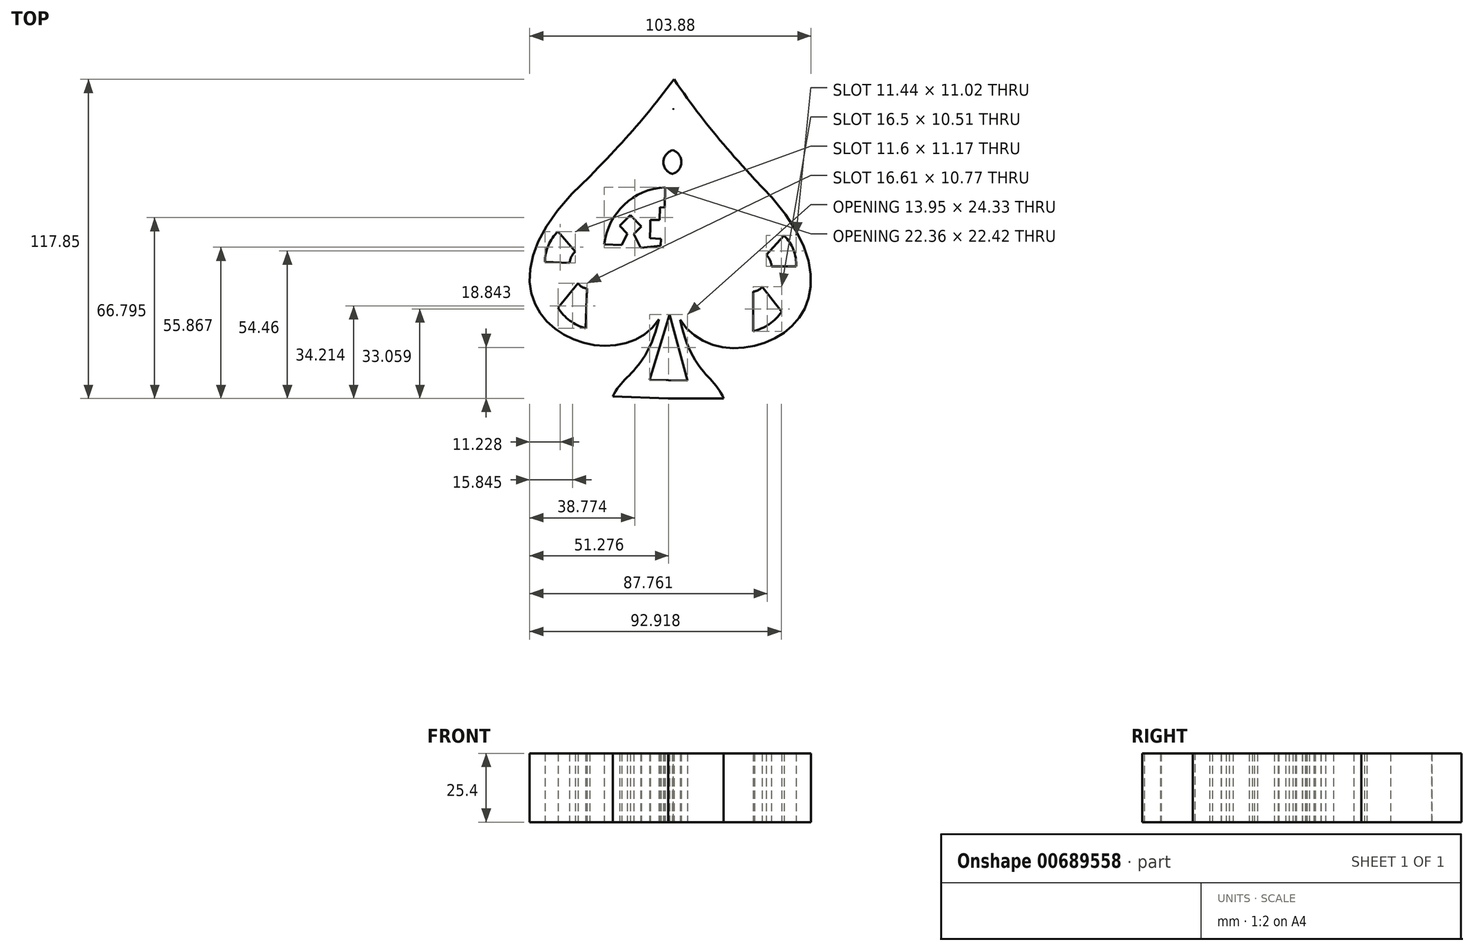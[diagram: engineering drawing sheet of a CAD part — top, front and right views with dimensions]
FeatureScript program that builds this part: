
annotation { "Feature Type Name" : "Feature", "Feature Type Description" : "" }
export const myFeature = defineFeature(function(context is Context, id is Id, definition is map)
    precondition{}
    {
        {
            var Q0;
            Q0=qCreatedBy(makeId("Top.planeOp"),FACE);
            var sketch = newSketch(context, id + "F0", { "sketchPlane" : qUnion([Q0])});
            skFitSpline(sketch, "E0", {"points": [v(-2.53, -37.9) * mm, v(-18.56, -8.8) * mm], "startDerivative": vector(-10, 25.18) * mm, "endDerivative": vector(-11.98, 58.7) * mm});
            skFitSpline(sketch, "E1", {"points": [v(-18.56, -8.8) * mm, v(8.92, 43.01) * mm], "startDerivative": vector(48.1, -79.64) * mm, "endDerivative": vector(-160.88, 156.33) * mm});
            skFitSpline(sketch, "E2", {"points": [v(8.92, 43.01) * mm, v(-20.9, 79.96) * mm], "startDerivative": vector(-37.04, 40.28) * mm, "endDerivative": vector(-28.87, 41.7) * mm});
            skLineSegment(sketch, "E3", {"start": v(-73.33, 8.06) * mm, "end": v(29.07, 0) * mm, "construction": true});
            skLineSegment(sketch, "E4", {"start": v(-2.53, -37.9) * mm, "end": v(-43.46, -37.9) * mm, "construction": true});
            skLineSegment(sketch, "E5", {"start": v(-23, -37.9) * mm, "end": v(-2.53, -37.9) * mm});
            skLineSegment(sketch, "E6", {"start": v(-23, -37.9) * mm, "end": v(-20.9, 79.96) * mm, "construction": true});
            skFitSpline(sketch, "E7.MirrorCS", {"points": [v(-52, 44.1) * mm, v(-20.9, 79.96) * mm], "startDerivative": vector(38.45, 38.94) * mm, "endDerivative": vector(30.34, 40.65) * mm});
            skFitSpline(sketch, "E8.MirrorCS", {"points": [v(-26.39, -8.66) * mm, v(-52, 44.1) * mm], "startDerivative": vector(-50.9, -77.88) * mm, "endDerivative": vector(166.34, 150.5) * mm});
            skFitSpline(sketch, "E9.MirrorCS", {"points": [v(-43.45, -37.16) * mm, v(-26.39, -8.66) * mm], "startDerivative": vector(10.89, 24.8) * mm, "endDerivative": vector(14.06, 58.23) * mm});
            skLineSegment(sketch, "E10.MirrorCS", {"start": v(-23, -37.9) * mm, "end": v(-43.45, -37.16) * mm});
            skFitSpline(sketch, "E11", {"points": [v(-22.32, 0) * mm, v(7.76, 41.99) * mm], "startDerivative": vector(35, -98.07) * mm, "endDerivative": vector(-155.79, 159.42) * mm});
            skLineSegment(sketch, "E12", {"start": v(7.76, 41.99) * mm, "end": v(-20.97, 75.69) * mm});
            skFitSpline(sketch, "E13.MirrorCS", {"points": [v(-22.32, 0) * mm, v(-50.89, 43.03) * mm], "startDerivative": vector(-38.47, -96.76) * mm, "endDerivative": vector(161.36, 153.78) * mm});
            skLineSegment(sketch, "E14.MirrorCS", {"start": v(-50.89, 43.03) * mm, "end": v(-20.97, 75.69) * mm});
            skFitSpline(sketch, "E15", {"points": [v(-21.1, 69) * mm, v(-12.63, 48.2) * mm], "startDerivative": vector(-3.17, 1.85) * mm, "endDerivative": vector(-12.5, -47.35) * mm});
            skFitSpline(sketch, "E16", {"points": [v(-12.63, 48.2) * mm, v(4.86, 35.93) * mm], "startDerivative": vector(24.47, -10.82) * mm, "endDerivative": vector(17.62, -20.68) * mm});
            skLineSegment(sketch, "E17", {"start": v(4.86, 35.93) * mm, "end": v(8.75, 35.43) * mm});
            skLineSegment(sketch, "E18", {"start": v(8.75, 35.43) * mm, "end": v(12.5, 31.25) * mm});
            skFitSpline(sketch, "E19", {"points": [v(12.5, 31.25) * mm, v(4.93, -2.27) * mm], "startDerivative": vector(-13.3, -42.42) * mm, "endDerivative": vector(-3.8, -40.26) * mm});
            skLineSegment(sketch, "E20", {"start": v(4.93, -2.27) * mm, "end": v(-17.9, -2.27) * mm});
            skLineSegment(sketch, "E21", {"start": v(-17.9, -2.27) * mm, "end": v(-22.3, 1.14) * mm});
            skLineSegment(sketch, "E22", {"start": v(-22.3, 1.14) * mm, "end": v(1.58, 0.9) * mm});
            skFitSpline(sketch, "E23", {"points": [v(1.58, 0.9) * mm, v(9.1, 30.71) * mm], "startDerivative": vector(0.02, 34.28) * mm, "endDerivative": vector(0.64, 27.66) * mm});
            skLineSegment(sketch, "E24", {"start": v(9.1, 30.71) * mm, "end": v(3.9, 31.77) * mm});
            skFitSpline(sketch, "E25", {"points": [v(3.9, 31.77) * mm, v(-17.82, 45.13) * mm], "startDerivative": vector(-2.54, 4.45) * mm, "endDerivative": vector(-44.2, 0.64) * mm});
            skFitSpline(sketch, "E26", {"points": [v(-17.82, 45.13) * mm, v(-19.45, 54.64) * mm], "startDerivative": vector(6.8, 6.6) * mm, "endDerivative": vector(-16.6, 7.97) * mm});
            skFitSpline(sketch, "E27", {"points": [v(-19.45, 54.64) * mm, v(-18.91, 55.61) * mm], "startDerivative": vector(1.1, 0.75) * mm, "endDerivative": vector(0.26, 1.43) * mm});
            skLineSegment(sketch, "E28", {"start": v(-18.91, 55.61) * mm, "end": v(-15.88, 55.02) * mm});
            skLineSegment(sketch, "E29", {"start": v(-15.88, 55.02) * mm, "end": v(-15.16, 58.67) * mm});
            skLineSegment(sketch, "E30", {"start": v(-15.16, 58.67) * mm, "end": v(-16.2, 58.69) * mm});
            skLineSegment(sketch, "E31", {"start": v(-16.2, 58.69) * mm, "end": v(-16.2, 60.6) * mm});
            skLineSegment(sketch, "E32", {"start": v(-16.2, 60.6) * mm, "end": v(-17.81, 60.63) * mm});
            skLineSegment(sketch, "E33", {"start": v(-17.81, 60.63) * mm, "end": v(-17.71, 62.36) * mm});
            skLineSegment(sketch, "E34", {"start": v(-17.71, 62.36) * mm, "end": v(-19.06, 62.48) * mm});
            skLineSegment(sketch, "E35", {"start": v(-19.06, 62.48) * mm, "end": v(-19.06, 64.14) * mm});
            skLineSegment(sketch, "E36", {"start": v(-19.06, 64.14) * mm, "end": v(-21.17, 64.57) * mm});
            skLineSegment(sketch, "E37.MirrorCS", {"start": v(-23.3, 64.21) * mm, "end": v(-21.17, 64.57) * mm});
            skLineSegment(sketch, "E38.MirrorCS", {"start": v(-23.35, 62.55) * mm, "end": v(-23.3, 64.21) * mm});
            skLineSegment(sketch, "E39.MirrorCS", {"start": v(-24.7, 62.49) * mm, "end": v(-23.35, 62.55) * mm});
            skLineSegment(sketch, "E40.MirrorCS", {"start": v(-24.67, 60.75) * mm, "end": v(-24.7, 62.49) * mm});
            skLineSegment(sketch, "E41.MirrorCS", {"start": v(-26.29, 60.78) * mm, "end": v(-24.67, 60.75) * mm});
            skLineSegment(sketch, "E42.MirrorCS", {"start": v(-26.36, 58.87) * mm, "end": v(-26.29, 60.78) * mm});
            skLineSegment(sketch, "E43.MirrorCS", {"start": v(-27.38, 58.89) * mm, "end": v(-26.36, 58.87) * mm});
            skLineSegment(sketch, "E44.MirrorCS", {"start": v(-26.8, 55.21) * mm, "end": v(-27.38, 58.89) * mm});
            skLineSegment(sketch, "E45.MirrorCS", {"start": v(-23.75, 55.7) * mm, "end": v(-26.8, 55.21) * mm});
            skFitSpline(sketch, "E46.MirrorCS", {"points": [v(-23.24, 54.71) * mm, v(-23.75, 55.7) * mm], "startDerivative": vector(-1.07, 0.79) * mm, "endDerivative": vector(-0.2, 1.44) * mm});
            skFitSpline(sketch, "E47.MirrorCS", {"points": [v(-25.2, 45.26) * mm, v(-23.24, 54.71) * mm], "startDerivative": vector(-6.57, 6.83) * mm, "endDerivative": vector(16.88, 7.38) * mm});
            skFitSpline(sketch, "E48.MirrorCS", {"points": [v(-47.4, 32.69) * mm, v(-25.2, 45.26) * mm], "startDerivative": vector(2.7, 4.36) * mm, "endDerivative": vector(44.19, -0.94) * mm});
            skLineSegment(sketch, "E49.MirrorCS", {"start": v(-52.62, 31.81) * mm, "end": v(-47.4, 32.69) * mm});
            skFitSpline(sketch, "E50.MirrorCS", {"points": [v(-46.17, 1.74) * mm, v(-52.62, 31.81) * mm], "startDerivative": vector(1.2, 34.26) * mm, "endDerivative": vector(0.35, 27.66) * mm});
            skLineSegment(sketch, "E51.MirrorCS", {"start": v(-22.3, 1.14) * mm, "end": v(-46.17, 1.74) * mm});
            skLineSegment(sketch, "E52.MirrorCS", {"start": v(-26.81, -2.11) * mm, "end": v(-22.3, 1.14) * mm});
            skLineSegment(sketch, "E53.MirrorCS", {"start": v(-49.63, -1.3) * mm, "end": v(-26.81, -2.11) * mm});
            skFitSpline(sketch, "E54.MirrorCS", {"points": [v(-56.01, 32.47) * mm, v(-49.63, -1.3) * mm], "startDerivative": vector(11.78, -42.87) * mm, "endDerivative": vector(2.37, -40.37) * mm});
            skLineSegment(sketch, "E55.MirrorCS", {"start": v(-52.1, 36.52) * mm, "end": v(-56.01, 32.47) * mm});
            skLineSegment(sketch, "E56.MirrorCS", {"start": v(-48.2, 36.87) * mm, "end": v(-52.1, 36.52) * mm});
            skFitSpline(sketch, "E57.MirrorCS", {"points": [v(-30.29, 48.51) * mm, v(-48.2, 36.87) * mm], "startDerivative": vector(-24.84, -9.94) * mm, "endDerivative": vector(-18.34, -20.04) * mm});
            skFitSpline(sketch, "E58.MirrorCS", {"points": [v(-21.1, 69) * mm, v(-30.29, 48.51) * mm], "startDerivative": vector(3.23, 1.74) * mm, "endDerivative": vector(10.81, -47.77) * mm});
            skArc(sketch, "E59", {"start": v(-21.52, 45) * mm, "mid": v(-18.12, 49.33) * mm, "end": v(-21.36, 53.79) * mm});
            skArc(sketch, "E60", {"start": v(2.89, 29.49) * mm, "mid": v(-7.22, 40.2) * mm, "end": v(-21.54, 43.65) * mm});
            skLineSegment(sketch, "E61", {"start": v(2.89, 29.49) * mm, "end": v(6.98, 28.8) * mm});
            skLineSegment(sketch, "E62", {"start": v(6.98, 28.8) * mm, "end": v(6.61, 27) * mm});
            skLineSegment(sketch, "E63", {"start": v(6.61, 27) * mm, "end": v(2.1, 27.63) * mm});
            skArc(sketch, "E64", {"start": v(2.1, 27.63) * mm, "mid": v(-7.57, 38.43) * mm, "end": v(-21.57, 42.2) * mm});
            skLineSegment(sketch, "E65", {"start": v(-19.02, 40.02) * mm, "end": v(-19.15, 32.56) * mm});
            skLineSegment(sketch, "E66", {"start": v(-19.15, 32.56) * mm, "end": v(-17.43, 32.53) * mm});
            skLineSegment(sketch, "E67", {"start": v(-17.43, 32.53) * mm, "end": v(-17.51, 27.87) * mm});
            skLineSegment(sketch, "E68", {"start": v(-17.51, 27.87) * mm, "end": v(-14.09, 27.8) * mm});
            skLineSegment(sketch, "E69", {"start": v(-14.09, 27.8) * mm, "end": v(-14.14, 25.18) * mm});
            skLineSegment(sketch, "E70", {"start": v(-14.14, 25.18) * mm, "end": v(-14.14, 20.98) * mm});
            skLineSegment(sketch, "E71", {"start": v(-14.14, 20.98) * mm, "end": v(-18.2, 20.98) * mm});
            skLineSegment(sketch, "E72", {"start": v(-18.2, 20.98) * mm, "end": v(-18.2, 18.43) * mm});
            skLineSegment(sketch, "E73", {"start": v(-18.2, 18.43) * mm, "end": v(-10.92, 17.3) * mm});
            skLineSegment(sketch, "E74", {"start": v(-10.92, 17.3) * mm, "end": v(-8.1, 22.3) * mm});
            skLineSegment(sketch, "E75", {"start": v(-8.1, 22.3) * mm, "end": v(-10.89, 25.18) * mm});
            skLineSegment(sketch, "E76", {"start": v(-10.89, 25.18) * mm, "end": v(-6.67, 29.26) * mm});
            skLineSegment(sketch, "E77", {"start": v(-6.67, 29.26) * mm, "end": v(-2.8, 25.25) * mm});
            skLineSegment(sketch, "E78", {"start": v(-2.8, 25.25) * mm, "end": v(-5.78, 22.36) * mm});
            skLineSegment(sketch, "E79", {"start": v(-5.78, 22.36) * mm, "end": v(-3.84, 18.15) * mm});
            skLineSegment(sketch, "E80", {"start": v(-3.84, 18.15) * mm, "end": v(2.58, 18.15) * mm});
            skArc(sketch, "E81", {"start": v(2.58, 18.15) * mm, "mid": v(-4.22, 33.04) * mm, "end": v(-19.02, 40.02) * mm});
            skArc(sketch, "E82.MirrorCS", {"start": v(-46.46, 30.37) * mm, "mid": v(-35.98, 40.72) * mm, "end": v(-21.54, 43.65) * mm});
            skLineSegment(sketch, "E83.MirrorCS", {"start": v(-46.46, 30.37) * mm, "end": v(-50.58, 29.82) * mm});
            skArc(sketch, "E84.MirrorCS", {"start": v(-21.52, 45) * mm, "mid": v(-24.76, 49.45) * mm, "end": v(-21.36, 53.79) * mm});
            skLineSegment(sketch, "E85.MirrorCS", {"start": v(-50.58, 29.82) * mm, "end": v(-50.28, 28) * mm});
            skLineSegment(sketch, "E86.MirrorCS", {"start": v(-50.28, 28) * mm, "end": v(-45.75, 28.48) * mm});
            skArc(sketch, "E87.MirrorCS", {"start": v(-45.75, 28.48) * mm, "mid": v(-35.7, 38.93) * mm, "end": v(-21.57, 42.2) * mm});
            skArc(sketch, "E88.MirrorCS", {"start": v(-46.56, 19.03) * mm, "mid": v(-39.24, 33.67) * mm, "end": v(-24.2, 40.12) * mm});
            skLineSegment(sketch, "E89.MirrorCS", {"start": v(-24.2, 40.12) * mm, "end": v(-24.33, 32.65) * mm});
            skLineSegment(sketch, "E90.MirrorCS", {"start": v(-24.33, 32.65) * mm, "end": v(-26.05, 32.68) * mm});
            skLineSegment(sketch, "E91.MirrorCS", {"start": v(-26.05, 32.68) * mm, "end": v(-26.13, 28.02) * mm});
            skLineSegment(sketch, "E92.MirrorCS", {"start": v(-26.13, 28.02) * mm, "end": v(-29.56, 28.08) * mm});
            skLineSegment(sketch, "E93.MirrorCS", {"start": v(-29.56, 28.08) * mm, "end": v(-29.6, 25.45) * mm});
            skLineSegment(sketch, "E94.MirrorCS", {"start": v(-29.6, 25.45) * mm, "end": v(-29.75, 21.26) * mm});
            skLineSegment(sketch, "E95.MirrorCS", {"start": v(-29.75, 21.26) * mm, "end": v(-25.7, 21.12) * mm});
            skLineSegment(sketch, "E96.MirrorCS", {"start": v(-25.7, 21.12) * mm, "end": v(-25.8, 18.57) * mm});
            skLineSegment(sketch, "E97.MirrorCS", {"start": v(-25.8, 18.57) * mm, "end": v(-33.1, 17.7) * mm});
            skLineSegment(sketch, "E98.MirrorCS", {"start": v(-33.1, 17.7) * mm, "end": v(-35.74, 22.8) * mm});
            skLineSegment(sketch, "E99.MirrorCS", {"start": v(-35.74, 22.8) * mm, "end": v(-32.85, 25.57) * mm});
            skLineSegment(sketch, "E100.MirrorCS", {"start": v(-32.85, 25.57) * mm, "end": v(-36.92, 29.8) * mm});
            skLineSegment(sketch, "E101.MirrorCS", {"start": v(-36.92, 29.8) * mm, "end": v(-40.93, 25.93) * mm});
            skLineSegment(sketch, "E102.MirrorCS", {"start": v(-40.93, 25.93) * mm, "end": v(-38.05, 22.93) * mm});
            skLineSegment(sketch, "E103.MirrorCS", {"start": v(-38.05, 22.93) * mm, "end": v(-40.14, 18.8) * mm});
            skLineSegment(sketch, "E104.MirrorCS", {"start": v(-40.14, 18.8) * mm, "end": v(-46.56, 19.03) * mm});
            skLineSegment(sketch, "E105.bottom", {"start": v(-22.06, 14.7) * mm, "end": v(0.65, 14.7) * mm});
            skLineSegment(sketch, "E105.top", {"start": v(-22.06, 9.84) * mm, "end": v(0.65, 9.84) * mm});
            skLineSegment(sketch, "E105.right", {"start": v(0.65, 14.7) * mm, "end": v(0.65, 9.84) * mm});
            skLineSegment(sketch, "E106.bottom", {"start": v(-22.2, 7.26) * mm, "end": v(0, 7.26) * mm});
            skLineSegment(sketch, "E106.top", {"start": v(-22.28, 2.29) * mm, "end": v(0, 2.29) * mm});
            skLineSegment(sketch, "E106.right", {"start": v(0, 7.26) * mm, "end": v(0, 2.29) * mm});
            skLineSegment(sketch, "E107.MirrorCS", {"start": v(-22.06, 14.7) * mm, "end": v(-44.76, 15.5) * mm});
            skLineSegment(sketch, "E108.MirrorCS", {"start": v(-22.23, 9.85) * mm, "end": v(-44.93, 10.66) * mm});
            skLineSegment(sketch, "E109.MirrorCS", {"start": v(-22.2, 7.26) * mm, "end": v(-44.37, 8.05) * mm});
            skLineSegment(sketch, "E110.MirrorCS", {"start": v(-22.28, 2.29) * mm, "end": v(-44.55, 3.08) * mm});
            skLineSegment(sketch, "E111.MirrorCS", {"start": v(-44.37, 8.05) * mm, "end": v(-44.55, 3.08) * mm});
            skLineSegment(sketch, "E112.MirrorCS", {"start": v(-44.76, 15.5) * mm, "end": v(-44.93, 10.66) * mm});
            skLineSegment(sketch, "E113.bottom", {"start": v(-5.78, 5.45) * mm, "end": v(-1.65, 5.45) * mm});
            skLineSegment(sketch, "E113.top", {"start": v(-5.78, 4.02) * mm, "end": v(-1.65, 4.02) * mm});
            skLineSegment(sketch, "E113.left", {"start": v(-5.78, 5.45) * mm, "end": v(-5.78, 4.02) * mm});
            skLineSegment(sketch, "E113.right", {"start": v(-1.65, 5.45) * mm, "end": v(-1.65, 4.02) * mm});
            skLineSegment(sketch, "E114.bottom", {"start": v(-12.25, 5.3) * mm, "end": v(-7.48, 5.3) * mm});
            skLineSegment(sketch, "E114.top", {"start": v(-12.25, 3.82) * mm, "end": v(-7.48, 3.82) * mm});
            skLineSegment(sketch, "E114.left", {"start": v(-12.25, 5.3) * mm, "end": v(-12.25, 3.82) * mm});
            skLineSegment(sketch, "E114.right", {"start": v(-7.48, 5.3) * mm, "end": v(-7.48, 3.82) * mm});
            skLineSegment(sketch, "E115.bottom", {"start": v(-19.15, 5.33) * mm, "end": v(-14.41, 5.33) * mm});
            skLineSegment(sketch, "E115.top", {"start": v(-19.15, 3.42) * mm, "end": v(-14.41, 3.42) * mm});
            skLineSegment(sketch, "E115.left", {"start": v(-19.15, 5.33) * mm, "end": v(-19.15, 3.42) * mm});
            skLineSegment(sketch, "E115.right", {"start": v(-14.41, 5.33) * mm, "end": v(-14.41, 3.42) * mm});
            skLineSegment(sketch, "E116.MirrorCS", {"start": v(-25.3, 5.44) * mm, "end": v(-30.04, 5.61) * mm});
            skLineSegment(sketch, "E117.MirrorCS", {"start": v(-25.3, 5.44) * mm, "end": v(-25.36, 3.53) * mm});
            skLineSegment(sketch, "E118.MirrorCS", {"start": v(-25.36, 3.53) * mm, "end": v(-30.1, 3.7) * mm});
            skLineSegment(sketch, "E119.MirrorCS", {"start": v(-30.04, 5.61) * mm, "end": v(-30.1, 3.7) * mm});
            skLineSegment(sketch, "E120.MirrorCS", {"start": v(-32.2, 5.65) * mm, "end": v(-32.25, 4.18) * mm});
            skLineSegment(sketch, "E121.MirrorCS", {"start": v(-32.2, 5.65) * mm, "end": v(-36.96, 5.82) * mm});
            skLineSegment(sketch, "E122.MirrorCS", {"start": v(-36.96, 5.82) * mm, "end": v(-37.01, 4.35) * mm});
            skLineSegment(sketch, "E123.MirrorCS", {"start": v(-32.25, 4.18) * mm, "end": v(-37.01, 4.35) * mm});
            skLineSegment(sketch, "E124.MirrorCS", {"start": v(-38.66, 6.04) * mm, "end": v(-38.71, 4.6) * mm});
            skLineSegment(sketch, "E125.MirrorCS", {"start": v(-38.66, 6.04) * mm, "end": v(-42.79, 6.18) * mm});
            skLineSegment(sketch, "E126.MirrorCS", {"start": v(-42.79, 6.18) * mm, "end": v(-42.84, 4.76) * mm});
            skLineSegment(sketch, "E127.MirrorCS", {"start": v(-38.71, 4.6) * mm, "end": v(-42.84, 4.76) * mm});
            skLineSegment(sketch, "E128", {"start": v(-37.68, 15.25) * mm, "end": v(-40.35, 12.52) * mm});
            skLineSegment(sketch, "E129", {"start": v(-40.35, 12.52) * mm, "end": v(-37.68, 10.4) * mm});
            skLineSegment(sketch, "E130", {"start": v(-37.68, 10.4) * mm, "end": v(-35.15, 12.52) * mm});
            skLineSegment(sketch, "E131", {"start": v(-35.15, 12.52) * mm, "end": v(-37.68, 15.25) * mm});
            skLineSegment(sketch, "E132", {"start": v(-29.44, 13.52) * mm, "end": v(-30.94, 12.05) * mm});
            skPoint(sketch, "E132.startSnap0", {"position": v(-29.44, 18.13) * mm});
            skLineSegment(sketch, "E133", {"start": v(-30.94, 12.05) * mm, "end": v(-29.44, 10.53) * mm});
            skLineSegment(sketch, "E134", {"start": v(-29.44, 10.53) * mm, "end": v(-27.89, 12.05) * mm});
            skLineSegment(sketch, "E135", {"start": v(-27.89, 12.05) * mm, "end": v(-29.44, 13.52) * mm});
            skLineSegment(sketch, "E136.MirrorCS", {"start": v(-16.33, 11.85) * mm, "end": v(-14.72, 13.26) * mm});
            skLineSegment(sketch, "E137.MirrorCS", {"start": v(-14.72, 13.26) * mm, "end": v(-13.28, 11.74) * mm});
            skLineSegment(sketch, "E138.MirrorCS", {"start": v(-13.28, 11.74) * mm, "end": v(-14.83, 10.27) * mm});
            skLineSegment(sketch, "E139.MirrorCS", {"start": v(-14.83, 10.27) * mm, "end": v(-16.33, 11.85) * mm});
            skLineSegment(sketch, "E140.MirrorCS", {"start": v(-9.06, 12.06) * mm, "end": v(-6.43, 14.7) * mm});
            skLineSegment(sketch, "E141.MirrorCS", {"start": v(-6.43, 14.7) * mm, "end": v(-3.85, 11.87) * mm});
            skLineSegment(sketch, "E142.MirrorCS", {"start": v(-3.85, 11.87) * mm, "end": v(-6.6, 9.84) * mm});
            skLineSegment(sketch, "E143.MirrorCS", {"start": v(-6.6, 9.84) * mm, "end": v(-9.06, 12.06) * mm});
            skArc(sketch, "E144", {"start": v(24.28, 10.85) * mm, "mid": v(23.24, 17.03) * mm, "end": v(19.83, 22.3) * mm});
            skLineSegment(sketch, "E145", {"start": v(24.28, 10.85) * mm, "end": v(15.16, 10.85) * mm});
            skLineSegment(sketch, "E146", {"start": v(19.83, 22.3) * mm, "end": v(13.26, 15.09) * mm});
            skArc(sketch, "E147", {"start": v(15.16, 10.85) * mm, "mid": v(14.6, 13.14) * mm, "end": v(13.26, 15.09) * mm});
            skArc(sketch, "E148", {"start": v(8.35, -13.08) * mm, "mid": v(14.29, -10.45) * mm, "end": v(18.87, -5.85) * mm});
            skLineSegment(sketch, "E149", {"start": v(8.35, -13.08) * mm, "end": v(8.35, 1.63) * mm});
            skLineSegment(sketch, "E150", {"start": v(18.87, -5.85) * mm, "end": v(11.72, 3.42) * mm});
            skPoint(sketch, "E150.endSnap0", {"position": v(-16.78, 3.42) * mm});
            skArc(sketch, "E151", {"start": v(8.35, 1.63) * mm, "mid": v(10.25, 2.12) * mm, "end": v(11.72, 3.42) * mm});
            skLineSegment(sketch, "E152.MirrorCS", {"start": v(-63.7, -4.38) * mm, "end": v(-56.22, 4.63) * mm});
            skArc(sketch, "E153.MirrorCS", {"start": v(-53.44, -11.98) * mm, "mid": v(-59.28, -9.14) * mm, "end": v(-63.7, -4.38) * mm});
            skArc(sketch, "E154.MirrorCS", {"start": v(-52.92, 2.72) * mm, "mid": v(-54.8, 3.28) * mm, "end": v(-56.22, 4.63) * mm});
            skLineSegment(sketch, "E155.MirrorCS", {"start": v(-53.44, -11.98) * mm, "end": v(-52.92, 2.72) * mm});
            skLineSegment(sketch, "E156.MirrorCS", {"start": v(-68.5, 12.5) * mm, "end": v(-59.4, 12.18) * mm});
            skArc(sketch, "E157.MirrorCS", {"start": v(-59.4, 12.18) * mm, "mid": v(-58.75, 14.45) * mm, "end": v(-57.34, 16.34) * mm});
            skLineSegment(sketch, "E158.MirrorCS", {"start": v(-63.65, 23.78) * mm, "end": v(-57.34, 16.34) * mm});
            skArc(sketch, "E159.MirrorCS", {"start": v(-68.5, 12.5) * mm, "mid": v(-67.25, 18.64) * mm, "end": v(-63.65, 23.78) * mm});
            skLineSegment(sketch, "E160", {"start": v(-23.48, -32.5) * mm, "end": v(-22.9, -32.5) * mm});
            skLineSegment(sketch, "E161.MirrorCS", {"start": v(-22.32, -32.51) * mm, "end": v(-22.9, -32.5) * mm});
            skLineSegment(sketch, "E162", {"start": v(-22.44, -6.88) * mm, "end": v(-15.9, -31.2) * mm});
            skLineSegment(sketch, "E163", {"start": v(-15.9, -31.2) * mm, "end": v(-22.87, -31.09) * mm});
            skLineSegment(sketch, "E164.MirrorCS", {"start": v(-22.44, -6.88) * mm, "end": v(-29.85, -30.96) * mm});
            skLineSegment(sketch, "E165.MirrorCS", {"start": v(-29.85, -30.96) * mm, "end": v(-22.87, -31.09) * mm});
            skSolve(sketch);
        }
        {
            var Q0;
            Q0=makeQuery(id+"F0.imprint","IMPRINT",FACE,{"disambiguationData":[TD([[makeQuery(id+"F0.imprint","IMPRINT",EDGE,{"derivedFrom":sQuery(id+"F0.wireOp",EDGE,"TR8coMyy-DoK1-fhJf-mkVZ-P4jdJu8iWF87")}),-1.0]])]});
            var Q1;
            Q1=makeQuery(id+"F0.imprint","IMPRINT",FACE,{"disambiguationData":[TD([[makeQuery(id+"F0.imprint","IMPRINT",EDGE,{"derivedFrom":sQuery(id+"F0.wireOp",EDGE,"E11")}),1.0]])]});
            var Q2;
            Q2=makeQuery(id+"F0.imprint","IMPRINT",FACE,{"disambiguationData":[TD([[makeQuery(id+"F0.imprint","IMPRINT",EDGE,{"derivedFrom":sQuery(id+"F0.wireOp",EDGE,"E22")}),1.0]])]});
            var Q3;
            Q3=makeQuery(id+"F0.imprint","IMPRINT",FACE,{"disambiguationData":[TD([[makeQuery(id+"F0.imprint","IMPRINT",EDGE,{"derivedFrom":sQuery(id+"F0.wireOp",EDGE,"E113.bottom")}),-1.0]])]});
            var Q4;
            Q4=makeQuery(id+"F0.imprint","IMPRINT",FACE,{"disambiguationData":[TD([[makeQuery(id+"F0.imprint","IMPRINT",EDGE,{"derivedFrom":sQuery(id+"F0.wireOp",EDGE,"E114.bottom")}),-1.0]])]});
            var Q5;
            Q5=makeQuery(id+"F0.imprint","IMPRINT",FACE,{"disambiguationData":[TD([[makeQuery(id+"F0.imprint","IMPRINT",EDGE,{"derivedFrom":sQuery(id+"F0.wireOp",EDGE,"E115.bottom")}),-1.0]])]});
            var Q6;
            Q6=makeQuery(id+"F0.imprint","IMPRINT",FACE,{"disambiguationData":[TD([[makeQuery(id+"F0.imprint","IMPRINT",EDGE,{"derivedFrom":sQuery(id+"F0.wireOp",EDGE,"E116.MirrorCS")}),1.0]])]});
            var Q7;
            Q7=makeQuery(id+"F0.imprint","IMPRINT",FACE,{"disambiguationData":[TD([[makeQuery(id+"F0.imprint","IMPRINT",EDGE,{"derivedFrom":sQuery(id+"F0.wireOp",EDGE,"E120.MirrorCS")}),-1.0]])]});
            var Q8;
            Q8=makeQuery(id+"F0.imprint","IMPRINT",FACE,{"disambiguationData":[TD([[makeQuery(id+"F0.imprint","IMPRINT",EDGE,{"derivedFrom":sQuery(id+"F0.wireOp",EDGE,"E124.MirrorCS")}),-1.0]])]});
            var Q9;
            Q9=makeQuery(id+"F0.imprint","IMPRINT",FACE,{"disambiguationData":[TD([[makeQuery(id+"F0.imprint","IMPRINT",EDGE,{"derivedFrom":sQuery(id+"F0.wireOp",EDGE,"E0")}),1.0]])]});
            var Q10;
            {var subQ0=sQuery(id+"F0.wireOp",EDGE,"E16");Q10=makeQuery(id+"F0.imprint","IMPRINT",FACE,{"disambiguationData":[TD([[makeQuery(id+"F0.imprint","IMPRINT",EDGE,{"derivedFrom":subQ0}),-1.0]])]});}
            var Q11;
            Q11=makeQuery(id+"F0.imprint","IMPRINT",FACE,{"disambiguationData":[TD([[makeQuery(id+"F0.imprint","IMPRINT",EDGE,{"derivedFrom":sQuery(id+"F0.wireOp",EDGE,"E106.bottom")}),-1.0]])]});
            var Q12;
            {var subQ1=sQuery(id+"F0.wireOp",EDGE,"E105.right");Q12=makeQuery(id+"F0.imprint","IMPRINT",FACE,{"disambiguationData":[TD([[makeQuery(id+"F0.imprint","IMPRINT",EDGE,{"derivedFrom":subQ1}),-1.0]])]});}
            var Q13;
            Q13=makeQuery(id+"F0.imprint","IMPRINT",FACE,{"disambiguationData":[TD([[makeQuery(id+"F0.imprint","IMPRINT",EDGE,{"derivedFrom":sQuery(id+"F0.wireOp",EDGE,"E140.MirrorCS")}),-1.0]])]});
            var Q14;
            Q14=makeQuery(id+"F0.imprint","IMPRINT",FACE,{"disambiguationData":[TD([[makeQuery(id+"F0.imprint","IMPRINT",EDGE,{"derivedFrom":sQuery(id+"F0.wireOp",EDGE,"E136.MirrorCS")}),-1.0]])]});
            var Q15;
            {var subQ0=sQuery(id+"F0.wireOp",EDGE,"E112.MirrorCS");Q15=makeQuery(id+"F0.imprint","IMPRINT",FACE,{"disambiguationData":[TD([[makeQuery(id+"F0.imprint","IMPRINT",EDGE,{"derivedFrom":subQ0}),1.0]])]});}
            var Q16;
            Q16=makeQuery(id+"F0.imprint","IMPRINT",FACE,{"disambiguationData":[TD([[makeQuery(id+"F0.imprint","IMPRINT",EDGE,{"derivedFrom":sQuery(id+"F0.wireOp",EDGE,"E128")}),1.0]])]});
            var Q17;
            Q17=makeQuery(id+"F0.imprint","IMPRINT",FACE,{"disambiguationData":[TD([[makeQuery(id+"F0.imprint","IMPRINT",EDGE,{"derivedFrom":sQuery(id+"F0.wireOp",EDGE,"E132")}),1.0]])]});
            var Q18;
            Q18=makeQuery(id+"F0.imprint","IMPRINT",FACE,{"disambiguationData":[TD([[makeQuery(id+"F0.imprint","IMPRINT",EDGE,{"derivedFrom":sQuery(id+"F0.wireOp",EDGE,"E65")}),1.0]])]});
            var Q19;
            Q19=makeQuery(id+"F0.imprint","IMPRINT",FACE,{"disambiguationData":[TD([[makeQuery(id+"F0.imprint","IMPRINT",EDGE,{"derivedFrom":sQuery(id+"F0.wireOp",EDGE,"E88.MirrorCS")}),-1.0]])]});
            var Q20;
            Q20=makeQuery(id+"F0.imprint","IMPRINT",FACE,{"disambiguationData":[TD([[makeQuery(id+"F0.imprint","IMPRINT",EDGE,{"derivedFrom":sQuery(id+"F0.wireOp",EDGE,"E60")}),1.0]])]});
            extrude(context, id + "F1", {"entities" : qUnion([Q0, Q1, Q2, Q3, Q4, Q5, Q6, Q7, Q8, Q9, Q10, Q11, Q12, Q13, Q14, Q15, Q16, Q17, Q18, Q19, Q20]), "depth" : 25.4 * mm, "offsetDistance" : 25.4 * mm});
        }
    });
